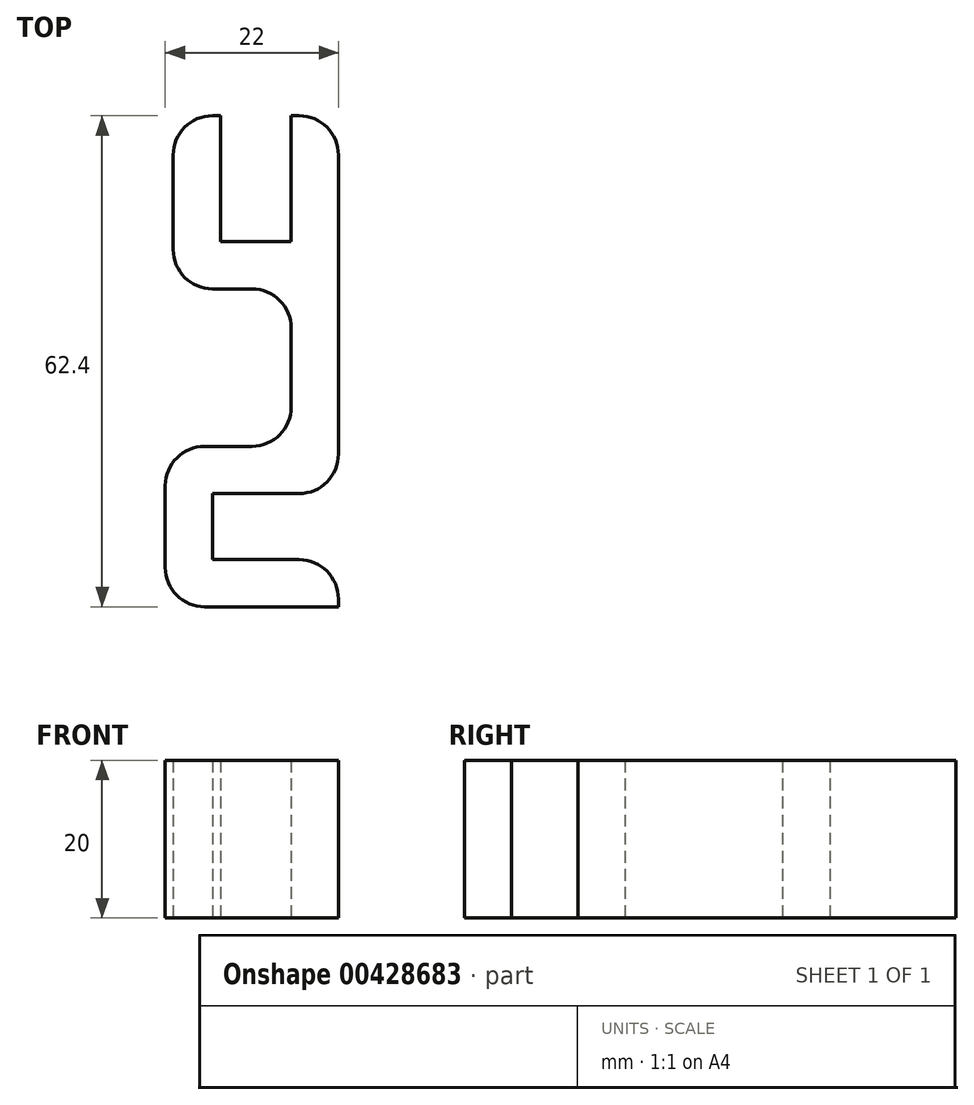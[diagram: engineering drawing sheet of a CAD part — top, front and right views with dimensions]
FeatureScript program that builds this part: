
annotation { "Feature Type Name" : "Feature", "Feature Type Description" : "" }
export const myFeature = defineFeature(function(context is Context, id is Id, definition is map)
    precondition{}
    {
        {
            var Q0;
            Q0=qCreatedBy(makeId("Top.planeOp"),FACE);
            var sketch = newSketch(context, id + "F0", { "sketchPlane" : qUnion([Q0])});
            skLineSegment(sketch, "E0.bottom", {"start": v(0, 0) * mm, "end": v(6, 0) * mm});
            skLineSegment(sketch, "E0.top", {"start": v(0, 20) * mm, "end": v(6, 20) * mm});
            skLineSegment(sketch, "E0.left", {"start": v(0, 0) * mm, "end": v(0, 20) * mm});
            skLineSegment(sketch, "E0.right", {"start": v(6, 0) * mm, "end": v(6, 20) * mm});
            skLineSegment(sketch, "E1.bottom", {"start": v(6, 20) * mm, "end": v(-15, 20) * mm});
            skLineSegment(sketch, "E1.top", {"start": v(6, 26) * mm, "end": v(-15, 26) * mm});
            skLineSegment(sketch, "E1.left", {"start": v(6, 20) * mm, "end": v(6, 26) * mm});
            skLineSegment(sketch, "E1.right", {"start": v(-15, 20) * mm, "end": v(-15, 26) * mm});
            skLineSegment(sketch, "E2.bottom", {"start": v(6, 26) * mm, "end": v(0, 26) * mm});
            skLineSegment(sketch, "E2.top", {"start": v(6, 42) * mm, "end": v(0, 42) * mm});
            skLineSegment(sketch, "E2.left", {"start": v(6, 26) * mm, "end": v(6, 42) * mm});
            skLineSegment(sketch, "E2.right", {"start": v(0, 26) * mm, "end": v(0, 42) * mm});
            skLineSegment(sketch, "E3.bottom", {"start": v(-15, 26) * mm, "end": v(-9, 26) * mm});
            skLineSegment(sketch, "E3.top", {"start": v(-15, 42) * mm, "end": v(-9, 42) * mm});
            skLineSegment(sketch, "E3.left", {"start": v(-15, 26) * mm, "end": v(-15, 42) * mm});
            skLineSegment(sketch, "E3.right", {"start": v(-9, 26) * mm, "end": v(-9, 42) * mm});
            skLineSegment(sketch, "E4.bottom", {"start": v(6, 0) * mm, "end": v(-16, 0) * mm});
            skLineSegment(sketch, "E4.top", {"start": v(6, -6) * mm, "end": v(-16, -6) * mm});
            skLineSegment(sketch, "E4.left", {"start": v(6, 0) * mm, "end": v(6, -6) * mm});
            skLineSegment(sketch, "E4.right", {"start": v(-16, 0) * mm, "end": v(-16, -6) * mm});
            skLineSegment(sketch, "E5.bottom", {"start": v(-16, -6) * mm, "end": v(-10, -6) * mm});
            skLineSegment(sketch, "E5.top", {"start": v(-16, -14.4) * mm, "end": v(-10, -14.4) * mm});
            skLineSegment(sketch, "E5.left", {"start": v(-16, -6) * mm, "end": v(-16, -14.4) * mm});
            skLineSegment(sketch, "E5.right", {"start": v(-10, -6) * mm, "end": v(-10, -14.4) * mm});
            skLineSegment(sketch, "E6.bottom", {"start": v(-16, -14.4) * mm, "end": v(6, -14.4) * mm});
            skLineSegment(sketch, "E6.top", {"start": v(-16, -20.4) * mm, "end": v(6, -20.4) * mm});
            skLineSegment(sketch, "E6.left", {"start": v(-16, -14.4) * mm, "end": v(-16, -20.4) * mm});
            skLineSegment(sketch, "E6.right", {"start": v(6, -14.4) * mm, "end": v(6, -20.4) * mm});
            skSolve(sketch);
        }
        {
            var Q0;
            Q0 = qSketchRegion(id + "F0", true);
            extrude(context, id + "F1", {"entities" : qUnion([Q0]), "depth" : 20 * mm});
        }
        {
            var Q0;
            Q0=makeQuery(id+"F1.opExtrude","SWEPT_EDGE",EDGE,{"disambiguationData":[OSD([sQuery(id+"F0.wireOp",EDGE,"E2.top"),sQuery(id+"F0.wireOp",EDGE,"E2.left")])]});
            var Q1;
            Q1=makeQuery(id+"F1.opExtrude","SWEPT_EDGE",EDGE,{"disambiguationData":[OSD([sQuery(id+"F0.wireOp",EDGE,"E3.top"),sQuery(id+"F0.wireOp",EDGE,"E3.left")])]});
            var Q2;
            Q2=makeQuery(id+"F1.opExtrude","SWEPT_EDGE",EDGE,{"disambiguationData":[OSD([sQuery(id+"F0.wireOp",EDGE,"E1.bottom"),sQuery(id+"F0.wireOp",EDGE,"E1.right")])]});
            var Q3;
            Q3=makeQuery(id+"F1.opExtrude","SWEPT_EDGE",EDGE,{"disambiguationData":[OSD([sQuery(id+"F0.wireOp",EDGE,"E4.bottom"),sQuery(id+"F0.wireOp",EDGE,"E4.right")])]});
            var Q4;
            Q4=makeQuery(id+"F1.opExtrude","SWEPT_EDGE",EDGE,{"disambiguationData":[OSD([sQuery(id+"F0.wireOp",EDGE,"E0.left"),sQuery(id+"F0.wireOp",EDGE,"E1.bottom")])]});
            var Q5;
            Q5=makeQuery(id+"F1.opExtrude","SWEPT_EDGE",EDGE,{"disambiguationData":[OSD([sQuery(id+"F0.wireOp",EDGE,"E0.left"),sQuery(id+"F0.wireOp",EDGE,"E4.bottom")])]});
            var Q6;
            Q6=makeQuery(id+"F1.opExtrude","SWEPT_EDGE",EDGE,{"disambiguationData":[OSD([sQuery(id+"F0.wireOp",EDGE,"E6.top"),sQuery(id+"F0.wireOp",EDGE,"E6.left")])]});
            var Q7;
            Q7=makeQuery(id+"F1.opExtrude","SWEPT_EDGE",EDGE,{"disambiguationData":[OSD([sQuery(id+"F0.wireOp",EDGE,"E4.top"),sQuery(id+"F0.wireOp",EDGE,"E4.left")])]});
            var Q8;
            Q8=makeQuery(id+"F1.opExtrude","SWEPT_EDGE",EDGE,{"disambiguationData":[OSD([sQuery(id+"F0.wireOp",EDGE,"E6.bottom"),sQuery(id+"F0.wireOp",EDGE,"E6.right")])]});
            fillet(context, id + "F2", {"entities" : qUnion([Q0, Q1, Q2, Q3, Q4, Q5, Q6, Q7, Q8]), "radius" : 5 * mm, "tangentPropagation" : true, "allowEdgeOverflow" : false});
        }
    });
